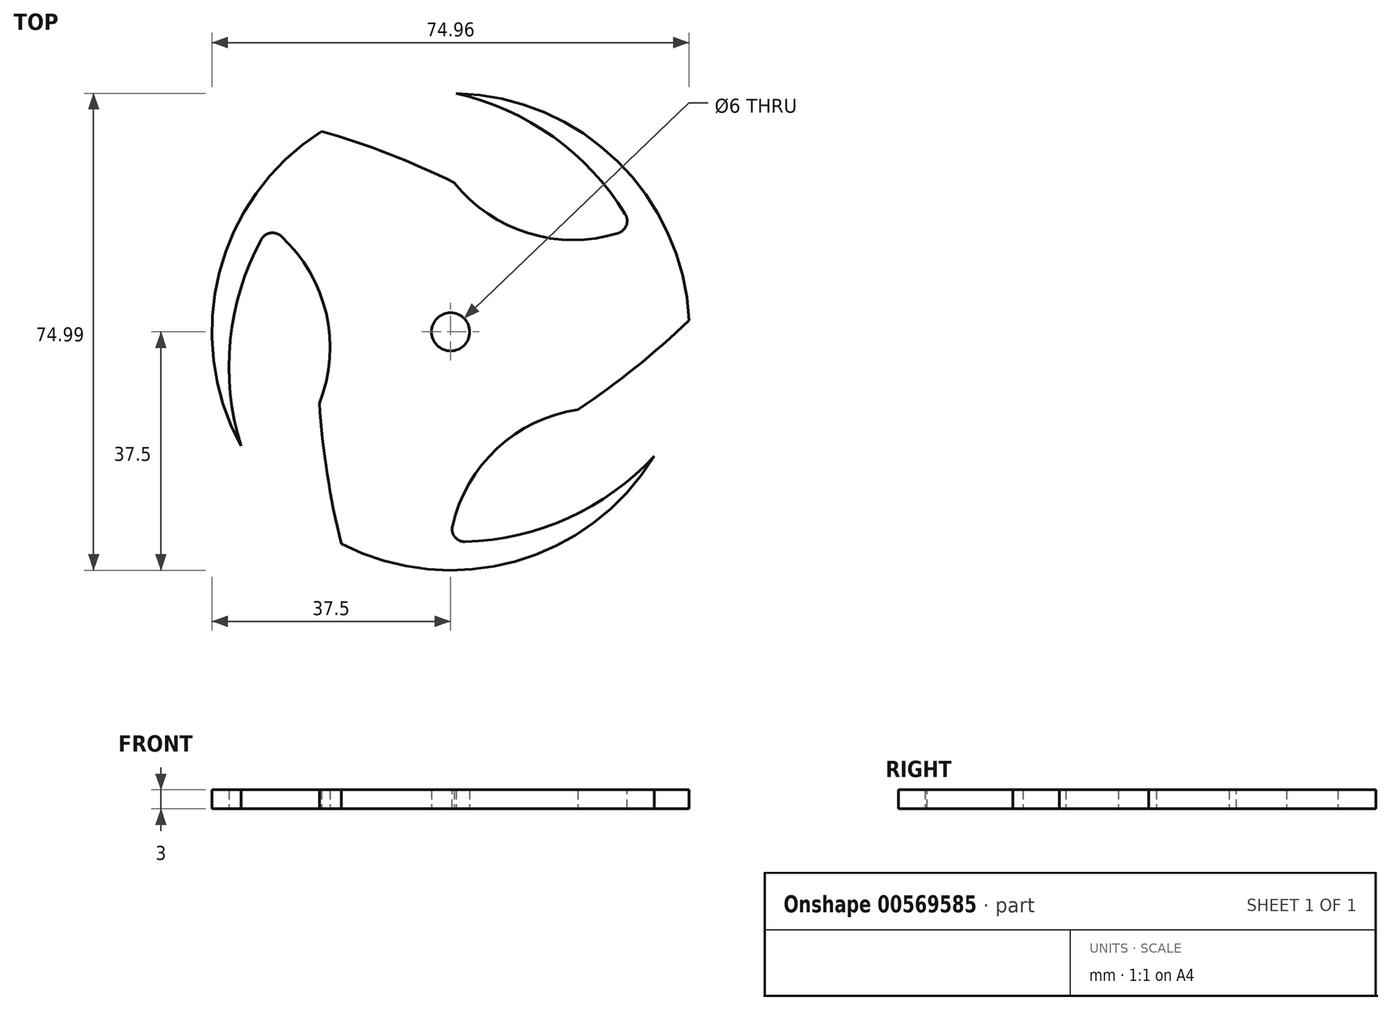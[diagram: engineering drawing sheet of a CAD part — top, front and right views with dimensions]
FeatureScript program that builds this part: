
annotation { "Feature Type Name" : "Feature", "Feature Type Description" : "" }
export const myFeature = defineFeature(function(context is Context, id is Id, definition is map)
    precondition{}
    {
        {
            var Q0;
            Q0=qCreatedBy(makeId("Top.planeOp"),FACE);
            var sketch = newSketch(context, id + "F0", { "sketchPlane" : qUnion([Q0])});
            skLineSegment(sketch, "E0.bottom", {"start": v(0, 0) * mm, "end": v(75, 0) * mm, "construction": true});
            skLineSegment(sketch, "E0.top", {"start": v(0, 75) * mm, "end": v(75, 75) * mm, "construction": true});
            skLineSegment(sketch, "E0.left", {"start": v(0, 0) * mm, "end": v(0, 75) * mm, "construction": true});
            skLineSegment(sketch, "E0.right", {"start": v(75, 0) * mm, "end": v(75, 75) * mm, "construction": true});
            skLineSegment(sketch, "E1", {"start": v(0, 75) * mm, "end": v(75, 0) * mm, "construction": true});
            skCircle(sketch, "E2", {"center": v(37.5, 37.5) * mm, "radius": 3 * mm});
            skCircle(sketch, "E3", {"center": v(37.5, 37.5) * mm, "radius": 37.5 * mm});
            skArc(sketch, "E4", {"start": v(8.98, 54.11) * mm, "mid": v(3.02, 37.3) * mm, "end": v(4.59, 19.53) * mm});
            skArc(sketch, "E5", {"start": v(16.9, 26.28) * mm, "mid": v(17.66, 41.54) * mm, "end": v(8.98, 54.11) * mm});
            skArc(sketch, "E6", {"start": v(16.9, 26.28) * mm, "mid": v(18.12, 15.15) * mm, "end": v(20.33, 4.16) * mm});
            skArc(sketch, "E7.1.0", {"start": v(57.51, 25.27) * mm, "mid": v(43.92, 18.3) * mm, "end": v(37.38, 4.5) * mm});
            skArc(sketch, "E7.1.1", {"start": v(57.51, 25.27) * mm, "mid": v(66.55, 31.9) * mm, "end": v(74.96, 39.3) * mm});
            skArc(sketch, "E7.1.2", {"start": v(37.38, 4.5) * mm, "mid": v(54.91, 7.74) * mm, "end": v(69.52, 17.98) * mm});
            skArc(sketch, "E7.2.0", {"start": v(38.08, 60.95) * mm, "mid": v(50.92, 52.66) * mm, "end": v(66.15, 53.9) * mm});
            skArc(sketch, "E7.2.1", {"start": v(38.08, 60.95) * mm, "mid": v(27.83, 65.46) * mm, "end": v(17.22, 69.04) * mm});
            skArc(sketch, "E7.2.2", {"start": v(66.15, 53.9) * mm, "mid": v(54.56, 67.46) * mm, "end": v(38.4, 74.99) * mm});
            skSolve(sketch);
        }
        {
            var Q0;
            Q0=makeQuery(id+"F0.imprint","IMPRINT",FACE,{"disambiguationData":[TD([[makeQuery(id+"F0.imprint","IMPRINT",EDGE,{"derivedFrom":sQuery(id+"F0.wireOp",EDGE,"E2")}),-1.0]])]});
            extrude(context, id + "F1", {"entities" : qUnion([Q0]), "depth" : 3 * mm, "offsetDistance" : 25 * mm});
        }
        {
            var Q0;
            Q0=makeQuery(id+"F1.opExtrude","SWEPT_EDGE",EDGE,{"disambiguationData":[OSD([sQuery(id+"F0.wireOp",EDGE,"E7.1.0"),sQuery(id+"F0.wireOp",EDGE,"E7.1.2")])]});
            fillet(context, id + "F2", {"entities" : qUnion([Q0]), "radius" : 2 * mm, "tangentPropagation" : true, "allowEdgeOverflow" : false});
        }
        {
            var Q0;
            Q0=makeQuery(id+"F1.opExtrude","SWEPT_EDGE",EDGE,{"disambiguationData":[OSD([sQuery(id+"F0.wireOp",EDGE,"E7.2.0"),sQuery(id+"F0.wireOp",EDGE,"E7.2.2")])]});
            var Q1;
            Q1=makeQuery(id+"F1.opExtrude","SWEPT_EDGE",EDGE,{"disambiguationData":[OSD([sQuery(id+"F0.wireOp",EDGE,"E4"),sQuery(id+"F0.wireOp",EDGE,"E5")])]});
            fillet(context, id + "F3", {"entities" : qUnion([Q0, Q1]), "radius" : 2 * mm, "tangentPropagation" : true, "allowEdgeOverflow" : false});
        }
    });
